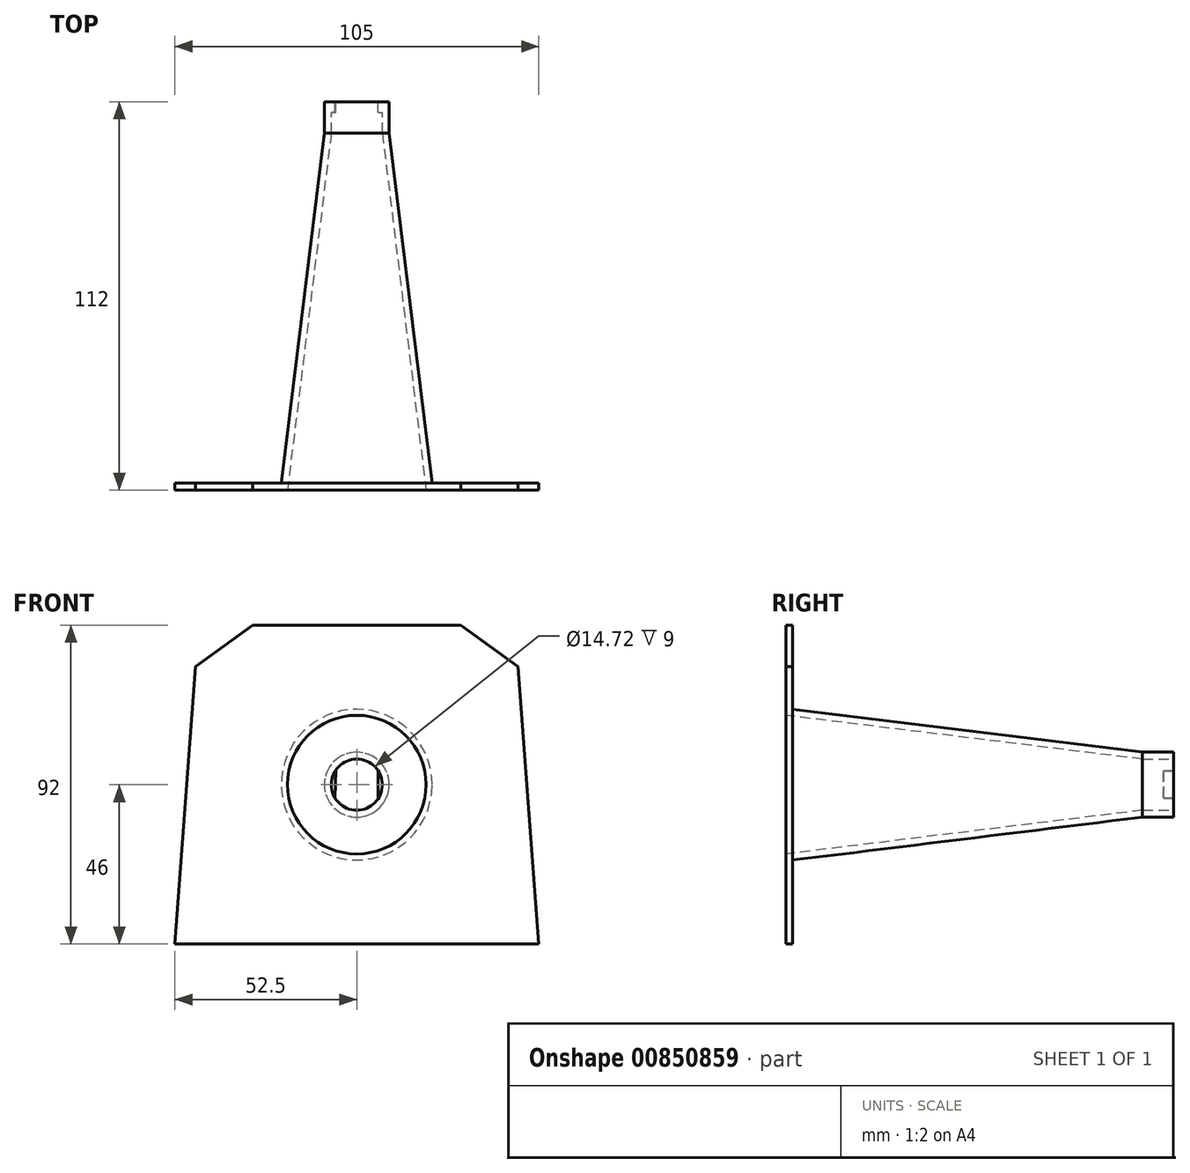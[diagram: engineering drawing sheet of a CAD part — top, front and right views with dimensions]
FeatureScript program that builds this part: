
annotation { "Feature Type Name" : "Feature", "Feature Type Description" : "" }
export const myFeature = defineFeature(function(context is Context, id is Id, definition is map)
    precondition{}
    {
        {
            var Q0;
            Q0=qCreatedBy(makeId("Front.planeOp"),FACE);
            var sketch = newSketch(context, id + "F0", { "sketchPlane" : qUnion([Q0])});
            skLineSegment(sketch, "E0", {"start": v(52.5, -46) * mm, "end": v(-52.5, -46) * mm});
            skLineSegment(sketch, "E1", {"start": v(-46.5, 34) * mm, "end": v(-52.5, -46) * mm});
            skLineSegment(sketch, "E2", {"start": v(46.5, 34) * mm, "end": v(52.5, -46) * mm});
            skLineSegment(sketch, "E3", {"start": v(-30, 46) * mm, "end": v(30, 46) * mm});
            skLineSegment(sketch, "E4", {"start": v(-46.5, 34) * mm, "end": v(-30, 46) * mm});
            skLineSegment(sketch, "E5", {"start": v(30, 46) * mm, "end": v(46.5, 34) * mm});
            skSolve(sketch);
        }
        {
            var Q0;
            Q0=makeQuery(id+"F0.imprint","IMPRINT",FACE,{"disambiguationData":[TD([[makeQuery(id+"F0.imprint","IMPRINT",EDGE,{"derivedFrom":sQuery(id+"F0.wireOp",EDGE,"E0")}),-1.0]])]});
            extrude(context, id + "F1", {"entities" : qUnion([Q0]), "oppositeDirection" : true, "depth" : 2 * mm, "offsetDistance" : 25 * mm});
        }
        {
            var Q0;
            Q0=qCreatedBy(makeId("Top.planeOp"),FACE);
            var sketch = newSketch(context, id + "F2", { "sketchPlane" : qUnion([Q0])});
            skLineSegment(sketch, "E6", {"start": v(0, 0) * mm, "end": v(-20, 0) * mm});
            skLineSegment(sketch, "E7", {"start": v(0, 163) * mm, "end": v(-20, 0) * mm});
            skLineSegment(sketch, "E8", {"start": v(0, 163) * mm, "end": v(0, 103) * mm});
            skLineSegment(sketch, "E9", {"start": v(0, 163) * mm, "end": v(0, 0) * mm});
            skLineSegment(sketch, "E10", {"start": v(-20, 0) * mm, "end": v(-22, 0) * mm});
            skLineSegment(sketch, "E11", {"start": v(-22, 0) * mm, "end": v(-0.56, 174.78) * mm});
            skLineSegment(sketch, "E12", {"start": v(0, 103) * mm, "end": v(-9.36, 103) * mm});
            skLineSegment(sketch, "E13", {"start": v(-9.36, 103) * mm, "end": v(-9.36, 112) * mm});
            skLineSegment(sketch, "E14", {"start": v(-9.36, 112) * mm, "end": v(0, 112) * mm});
            skLineSegment(sketch, "E15", {"start": v(-7.36, 103) * mm, "end": v(-7.36, 112) * mm});
            skSolve(sketch);
        }
        {
            var Q0;
            {var subQ0=sQuery(id+"F2.wireOp",EDGE,"E6");Q0=makeQuery(id+"F2.imprint","IMPRINT",FACE,{"disambiguationData":[TD([[makeQuery(id+"F2.imprint","IMPRINT",EDGE,{"derivedFrom":subQ0}),-1.0]])]});}
            var Q1;
            Q1=sQuery(id+"F2.wireOp",EDGE,"E9");
            revolve(context, id + "F3", {"operationType" : NewBodyOperationType.REMOVE, "surfaceOperationType" : NewSurfaceOperationType.NEW, "entities" : qUnion([Q0]), "axis" : qUnion([Q1]), "revolveType" : RevolveType.FULL});
        }
        {
            var Q0;
            {var subQ0=sQuery(id+"F2.wireOp",EDGE,"E10");Q0=makeQuery(id+"F2.imprint","IMPRINT",FACE,{"disambiguationData":[TD([[makeQuery(id+"F2.imprint","IMPRINT",EDGE,{"derivedFrom":subQ0}),-1.0]])]});}
            var Q1;
            {var subQ5=sQuery(id+"F2.wireOp",EDGE,"E15");Q1=makeQuery(id+"F2.imprint","IMPRINT",FACE,{"disambiguationData":[TD([[makeQuery(id+"F2.imprint","IMPRINT",EDGE,{"derivedFrom":subQ5}),1.0]])]});}
            var Q2;
            {var subQ0=sQuery(id+"F2.wireOp",EDGE,"E13");Q2=makeQuery(id+"F2.imprint","IMPRINT",FACE,{"disambiguationData":[TD([[makeQuery(id+"F2.imprint","IMPRINT",EDGE,{"derivedFrom":subQ0}),-1.0]])]});}
            var Q3;
            Q3=makeQuery(id+"F3.boolean.opBoolean","INTERSECT",EDGE,{"derivedFrom":[makeQuery(id+"F1.opExtrude","CAP_FACE",FACE,{"disambiguationData":[OSD([sQuery(id+"F0.wireOp",EDGE,"E0"),sQuery(id+"F0.wireOp",EDGE,"E1"),sQuery(id+"F0.wireOp",EDGE,"E2"),sQuery(id+"F0.wireOp",EDGE,"E3"),sQuery(id+"F0.wireOp",EDGE,"E4"),sQuery(id+"F0.wireOp",EDGE,"E5")])],"isStart":false}),makeQuery(id+"F3.opRevolve","SWEPT_FACE",FACE,{"disambiguationData":[OSD([sQuery(id+"F2.wireOp",EDGE,"E7")])]})]});
            revolve(context, id + "F4", {"operationType" : NewBodyOperationType.ADD, "surfaceOperationType" : NewSurfaceOperationType.NEW, "entities" : qUnion([Q0, Q1, Q2]), "axis" : qUnion([Q3]), "revolveType" : RevolveType.FULL});
        }
        {
            var Q0;
            Q0=makeQuery(id+"F4.opRevolve","SWEPT_FACE",FACE,{"disambiguationData":[OSD([sQuery(id+"F2.wireOp",EDGE,"E14")])]});
            var sketch = newSketch(context, id + "F5", { "sketchPlane" : qUnion([Q0])});
            skLineSegment(sketch, "E16", {"start": v(0, 0) * mm, "end": v(-6.2, 0) * mm});
            skLineSegment(sketch, "E17", {"start": v(-6.2, 0) * mm, "end": v(-6.2, 3.97) * mm});
            skLineSegment(sketch, "E18", {"start": v(-6.2, 3.97) * mm, "end": v(-6.2, -3.97) * mm});
            skLineSegment(sketch, "E19", {"start": v(0, 0) * mm, "end": v(6.2, 0) * mm});
            skLineSegment(sketch, "E20", {"start": v(6.09, 4.14) * mm, "end": v(6.3, -3.8) * mm});
            skSolve(sketch);
        }
        {
            var Q0;
            {var subQ0=sQuery(id+"F5.wireOp",EDGE,"E18");var subQ1=makeQuery(id+"F5.imprint","INTERSECT",VERTEX,{"derivedFrom":[sQuery(id+"F5.wireOp",EDGE,"E16"),subQ0]});Q0=makeQuery(id+"F5.imprint","IMPRINT",FACE,{"disambiguationData":[TD([[makeQuery(id+"F5.imprint","IMPRINT",EDGE,{"disambiguationData":[TD([[subQ1,1.0]])],"derivedFrom":subQ0}),-1.0]])]});}
            var Q1;
            {var subQ0=sQuery(id+"F5.wireOp",EDGE,"E20");var subQ1=makeQuery(id+"F5.imprint","INTERSECT",VERTEX,{"derivedFrom":[sQuery(id+"F5.wireOp",EDGE,"E19"),subQ0]});Q1=makeQuery(id+"F5.imprint","IMPRINT",FACE,{"disambiguationData":[TD([[makeQuery(id+"F5.imprint","IMPRINT",EDGE,{"disambiguationData":[TD([[subQ1,1.0]])],"derivedFrom":subQ0}),1.0]])]});}
            extrude(context, id + "F6", {"entities" : qUnion([Q0, Q1]), "operationType" : NewBodyOperationType.ADD, "oppositeDirection" : true, "depth" : 3 * mm, "offsetDistance" : 25 * mm});
        }
    });
